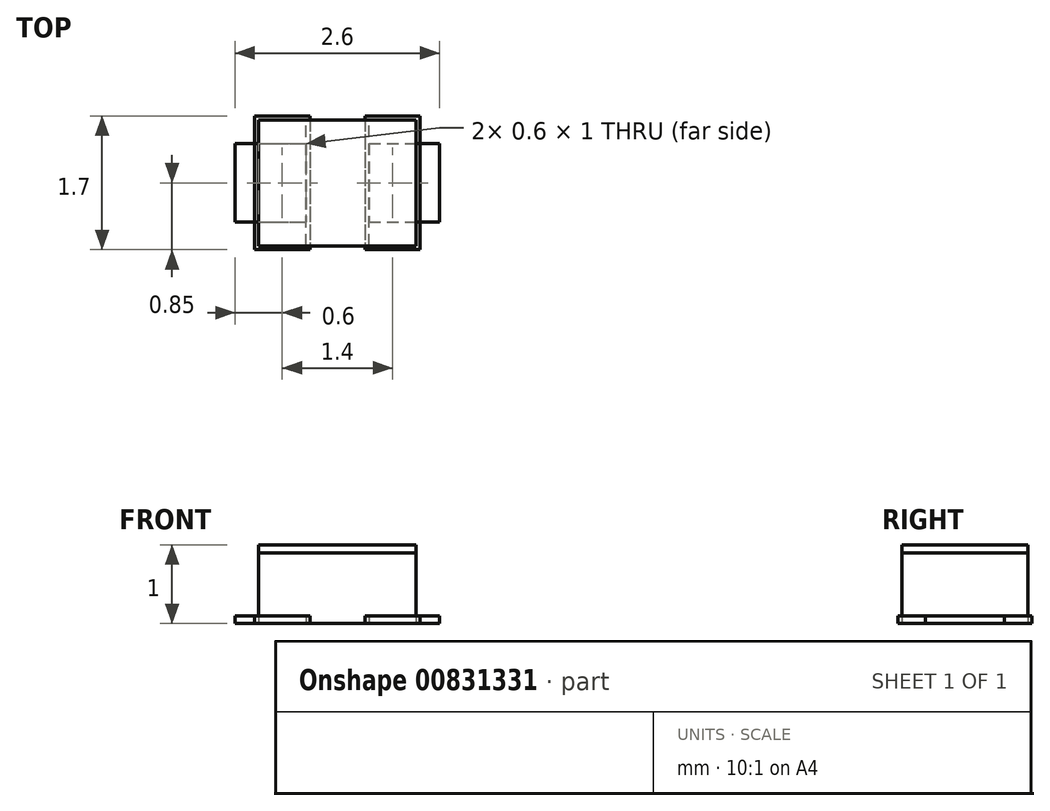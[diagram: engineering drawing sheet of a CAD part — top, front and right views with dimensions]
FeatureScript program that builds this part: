
annotation { "Feature Type Name" : "Feature", "Feature Type Description" : "" }
export const myFeature = defineFeature(function(context is Context, id is Id, definition is map)
    precondition{}
    {
        {
            var Q0;
            Q0=qCreatedBy(makeId("Top.planeOp"),FACE);
            var sketch = newSketch(context, id + "F0", { "sketchPlane" : qUnion([Q0])});
            skLineSegment(sketch, "E0.bottom", {"start": v(-1, -0.8) * mm, "end": v(1, -0.8) * mm});
            skLineSegment(sketch, "E0.top", {"start": v(-1, 0.8) * mm, "end": v(1, 0.8) * mm});
            skLineSegment(sketch, "E0.left", {"start": v(-1, -0.8) * mm, "end": v(-1, 0.8) * mm});
            skLineSegment(sketch, "E0.right", {"start": v(1, -0.8) * mm, "end": v(1, 0.8) * mm});
            skLineSegment(sketch, "E1", {"start": v(0, 0.8) * mm, "end": v(0, -0.8) * mm, "construction": true});
            skSolve(sketch);
        }
        {
            var Q0;
            Q0 = qSketchRegion(id + "F0", true);
            extrude(context, id + "F1", {"entities" : qUnion([Q0]), "depth" : 1 * mm, "offsetDistance" : 25 * mm});
        }
        {
            var Q0;
            Q0=makeQuery(id+"F1.opExtrude","CAP_FACE",FACE,{"disambiguationData":[OSD([sQuery(id+"F0.wireOp",EDGE,"E0.bottom"),sQuery(id+"F0.wireOp",EDGE,"E0.top"),sQuery(id+"F0.wireOp",EDGE,"E0.left"),sQuery(id+"F0.wireOp",EDGE,"E0.right")])],"isStart":true});
            var sketch = newSketch(context, id + "F2", { "sketchPlane" : qUnion([Q0])});
            skLineSegment(sketch, "E2.bottom", {"start": v(-1, 0.8) * mm, "end": v(-0.4, 0.8) * mm});
            skLineSegment(sketch, "E2.top", {"start": v(-1, -0.8) * mm, "end": v(-0.4, -0.8) * mm});
            skLineSegment(sketch, "E2.left", {"start": v(-1, 0.8) * mm, "end": v(-1, -0.8) * mm});
            skLineSegment(sketch, "E2.right", {"start": v(-0.4, 0.8) * mm, "end": v(-0.4, -0.8) * mm});
            skLineSegment(sketch, "E3.bottom", {"start": v(1, 0.8) * mm, "end": v(0.4, 0.8) * mm});
            skLineSegment(sketch, "E3.top", {"start": v(1, -0.8) * mm, "end": v(0.4, -0.8) * mm});
            skLineSegment(sketch, "E3.left", {"start": v(1, 0.8) * mm, "end": v(1, -0.8) * mm});
            skLineSegment(sketch, "E3.right", {"start": v(0.4, 0.8) * mm, "end": v(0.4, -0.8) * mm});
            skSolve(sketch);
        }
        {
            var Q0;
            Q0 = qSketchRegion(id + "F2", true);
            extrude(context, id + "F3", {"entities" : qUnion([Q0]), "operationType" : NewBodyOperationType.REMOVE, "oppositeDirection" : true, "depth" : .1 * mm, "offsetDistance" : 25 * mm});
        }
        {
            var Q0;
            Q0=qCreatedBy(makeId("Top.planeOp"),FACE);
            var sketch = newSketch(context, id + "F4", { "sketchPlane" : qUnion([Q0])});
            skLineSegment(sketch, "E4.bottom", {"start": v(-1.05, 0.85) * mm, "end": v(-0.35, 0.85) * mm});
            skLineSegment(sketch, "E4.top", {"start": v(-1.05, -0.85) * mm, "end": v(-0.35, -0.85) * mm});
            skLineSegment(sketch, "E4.left", {"start": v(-1.05, 0.85) * mm, "end": v(-1.05, -0.85) * mm});
            skLineSegment(sketch, "E4.right", {"start": v(-0.35, 0.85) * mm, "end": v(-0.35, -0.85) * mm});
            skLineSegment(sketch, "E5.bottom", {"start": v(0.35, 0.85) * mm, "end": v(1.05, 0.85) * mm});
            skLineSegment(sketch, "E5.top", {"start": v(0.35, -0.85) * mm, "end": v(1.05, -0.85) * mm});
            skLineSegment(sketch, "E5.left", {"start": v(0.35, 0.85) * mm, "end": v(0.35, -0.85) * mm});
            skLineSegment(sketch, "E5.right", {"start": v(1.05, 0.85) * mm, "end": v(1.05, -0.85) * mm});
            skLineSegment(sketch, "E6", {"start": v(0, 0) * mm, "end": v(-1.05, 0) * mm, "construction": true});
            skLineSegment(sketch, "E7", {"start": v(0, 0) * mm, "end": v(1.05, 0) * mm, "construction": true});
            skSolve(sketch);
        }
        {
            var Q0;
            Q0 = qSketchRegion(id + "F4", true);
            extrude(context, id + "F5", {"entities" : qUnion([Q0]), "depth" : .1 * mm, "offsetDistance" : 25 * mm});
        }
        {
            var Q0;
            Q0=qCreatedBy(makeId("Top.planeOp"),FACE);
            var sketch = newSketch(context, id + "F6", { "sketchPlane" : qUnion([Q0])});
            skLineSegment(sketch, "E8.bottom", {"start": v(-1, -0.8) * mm, "end": v(1, -0.8) * mm});
            skLineSegment(sketch, "E8.top", {"start": v(-1, 0.8) * mm, "end": v(1, 0.8) * mm});
            skLineSegment(sketch, "E8.left", {"start": v(-1, -0.8) * mm, "end": v(-1, 0.8) * mm});
            skLineSegment(sketch, "E8.right", {"start": v(1, -0.8) * mm, "end": v(1, 0.8) * mm});
            skLineSegment(sketch, "E9", {"start": v(0, 0.8) * mm, "end": v(0, -0.8) * mm, "construction": true});
            skSolve(sketch);
        }
        {
            var Q0;
            Q0 = qSketchRegion(id + "F6", true);
            extrude(context, id + "F7", {"entities" : qUnion([Q0]), "depth" : .9 * mm, "offsetDistance" : 25 * mm});
        }
        {
            var Q0;
            Q0=makeQuery(id+"F7.opExtrude","CAP_FACE",FACE,{"disambiguationData":[OSD([sQuery(id+"F6.wireOp",EDGE,"E8.bottom"),sQuery(id+"F6.wireOp",EDGE,"E8.top"),sQuery(id+"F6.wireOp",EDGE,"E8.left"),sQuery(id+"F6.wireOp",EDGE,"E8.right")])],"isStart":true});
            var sketch = newSketch(context, id + "F8", { "sketchPlane" : qUnion([Q0])});
            skLineSegment(sketch, "E10.bottom", {"start": v(-1, 0.5) * mm, "end": v(-0.4, 0.5) * mm});
            skLineSegment(sketch, "E10.top", {"start": v(-1, -0.5) * mm, "end": v(-0.4, -0.5) * mm});
            skLineSegment(sketch, "E10.left", {"start": v(-1, 0.5) * mm, "end": v(-1, -0.5) * mm});
            skLineSegment(sketch, "E10.right", {"start": v(-0.4, 0.5) * mm, "end": v(-0.4, -0.5) * mm});
            skLineSegment(sketch, "E11.bottom", {"start": v(1, 0.5) * mm, "end": v(0.4, 0.5) * mm});
            skLineSegment(sketch, "E11.top", {"start": v(1, -0.5) * mm, "end": v(0.4, -0.5) * mm});
            skLineSegment(sketch, "E11.left", {"start": v(1, 0.5) * mm, "end": v(1, -0.5) * mm});
            skLineSegment(sketch, "E11.right", {"start": v(0.4, 0.5) * mm, "end": v(0.4, -0.5) * mm});
            skLineSegment(sketch, "E12", {"start": v(-0.4, 0) * mm, "end": v(0, 0) * mm, "construction": true});
            skSolve(sketch);
        }
        {
            var Q0;
            Q0 = qSketchRegion(id + "F8", true);
            extrude(context, id + "F9", {"entities" : qUnion([Q0]), "operationType" : NewBodyOperationType.REMOVE, "oppositeDirection" : true, "depth" : .1 * mm, "offsetDistance" : 25 * mm});
        }
        {
            var Q0;
            Q0=qCreatedBy(makeId("Top.planeOp"),FACE);
            var sketch = newSketch(context, id + "F10", { "sketchPlane" : qUnion([Q0])});
            skLineSegment(sketch, "E13.bottom", {"start": v(-1.3, 0.5) * mm, "end": v(-0.4, 0.5) * mm});
            skLineSegment(sketch, "E13.top", {"start": v(-1.3, -0.5) * mm, "end": v(-0.4, -0.5) * mm});
            skLineSegment(sketch, "E13.left", {"start": v(-1.3, 0.5) * mm, "end": v(-1.3, -0.5) * mm});
            skLineSegment(sketch, "E13.right", {"start": v(-0.4, 0.5) * mm, "end": v(-0.4, -0.5) * mm});
            skLineSegment(sketch, "E14.bottom", {"start": v(0.4, 0.5) * mm, "end": v(1.3, 0.5) * mm});
            skLineSegment(sketch, "E14.top", {"start": v(0.4, -0.5) * mm, "end": v(1.3, -0.5) * mm});
            skLineSegment(sketch, "E14.left", {"start": v(0.4, 0.5) * mm, "end": v(0.4, -0.5) * mm});
            skLineSegment(sketch, "E14.right", {"start": v(1.3, 0.5) * mm, "end": v(1.3, -0.5) * mm});
            skLineSegment(sketch, "E15", {"start": v(-0.4, 0) * mm, "end": v(0, 0) * mm, "construction": true});
            skLineSegment(sketch, "E16", {"start": v(0, 0) * mm, "end": v(0.4, 0) * mm, "construction": true});
            skSolve(sketch);
        }
        {
            var Q0;
            Q0 = qSketchRegion(id + "F10", true);
            extrude(context, id + "F11", {"entities" : qUnion([Q0]), "depth" : .1 * mm, "offsetDistance" : 25 * mm});
        }
    });
